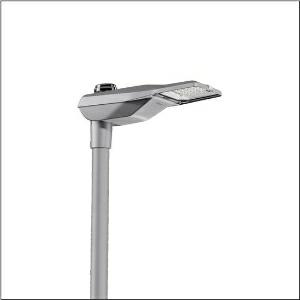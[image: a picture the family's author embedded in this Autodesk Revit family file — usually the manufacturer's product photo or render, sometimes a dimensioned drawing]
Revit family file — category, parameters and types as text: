
# Revit family: streetlight_sl_21_micro___st0_8a_5xe5c37n08cb_a39a
name_source: partatom
category: Lighting Fixtures
units: mm (PartAtom-declared; Revit-internal decimal feet)

## family parameters
Cut with Voids When Loaded = No
Host = Face
Light Source = No
Part Type = Normal
Room Calculation Point = No
Round Connector Dimension = Use Diameter
Shared = No

## types (1)
- --- (1 x LED, 2290 lm, 15.8 W, 3000K)
    Apparent Load = 16 VA
    CIE Flux Codes = 38 75 97 100 100
    Color Rendering = 70
    Color Temperature = 3000K
    Default Elevation = 1800 mm
    Description = Streetlight SL 21 micro, mast luminaire, primary light control with lens, of PMMA, primary optical cover: cover, of toughened safety glass, transparent, light distribution: ST0.8a, light emission: direct distribution, primary light characteristic: asymmetric, installation type: post-top, LED, 3G 1.5mm², High Power LED, rated luminous flux: 2.290lm, luminous efficacy: 145lm/W, light colour: 730, colour temperature: 3000K, control gear: NEMA (7pin), control: overheat protection, pre-setting: linear dimming characteristic, constant luminous flux control, time-dependent luminous flux control, flexible luminous flux parameterisation, mains connection: 230..240V, AC, 50/60Hz, connection cable pre-assembled, cable length: 6,5m, wiring characteristics: H07RN-F, start of lifetime: 16W, end of service life: 16W, reduction: 8W, luminaire housing, of diecast aluminium (EN AC-44300), powder-coated, SITECO metallic grey (DB 702S), corrosivity category C5 high according to DIN EN ISO 12944, multi-level sealing system, sealing non-destructively replaceable, inclination adjustable: 0°, 5°, 10°, 15°, length: 528mm, width: 235mm, height: 110mm, spigot size: 76/60mm (post-top), mounting height: 4..8m, protection rating (complete): IP66, insulation class (complete): insulation class I (protective earthing), certification: CE, ENEC, ENEC+, VDE, impact resistance: IK10, permissible operating ambient temperature for outdoor applications: -40..+50°C, standard-compliant lighting for roads and squares, packaging unit: 1 piece

Light Distribution: ST0.8a
    Height = 110 mm
    Lamp = 1 x LED
    Lamp Light Flux = 2290 lm
    Lamp Power = 15.8 W
    Lamp count = 1
    Length = 528 mm
    Luminous efficacy = 145 lm/W
    Manufacturer = Siteco
    ModVariant = No
    Model = 5XE5C37N08CB
    Number of Poles = 1
    OnlyDefault = Yes
    Power Factor = 1
    Product Name = Streetlight SL 21 micro | ST0.8a
    Product group = mast luminaire | pylon top
    ProductGroupID = 6100
    Protection Class = Protection class I
    Protection Degree = IP 66
    RLX_Detail_Level = 1
    RLX_Emergency_Light_Flux = 0 lm
    RLX_Emergency_Type = 0
    RLX_Emergency_Type_DB = No
    RlxData = <blob elided: 98701 chars, md5=4dfa523e>
    Socket = socket
    Standby Power = 0 W
    System Light Flux = 2290 lm
    System Power = 16 W
    Type Comments = factory setting: luminous flux: 100 % | dim-lin: 254 | 300 mA
    Type Image = l_1294375.jpg
    URL = http://relux.com
    VarID = @adj_133907
    Voltage = 0 V
    Weight = 0.00 kg
    Width = 235 mm

## geometry (parser evidence)
native form markers: Blend x4, Sweep x11
no freeform markers — native parametric forms only
